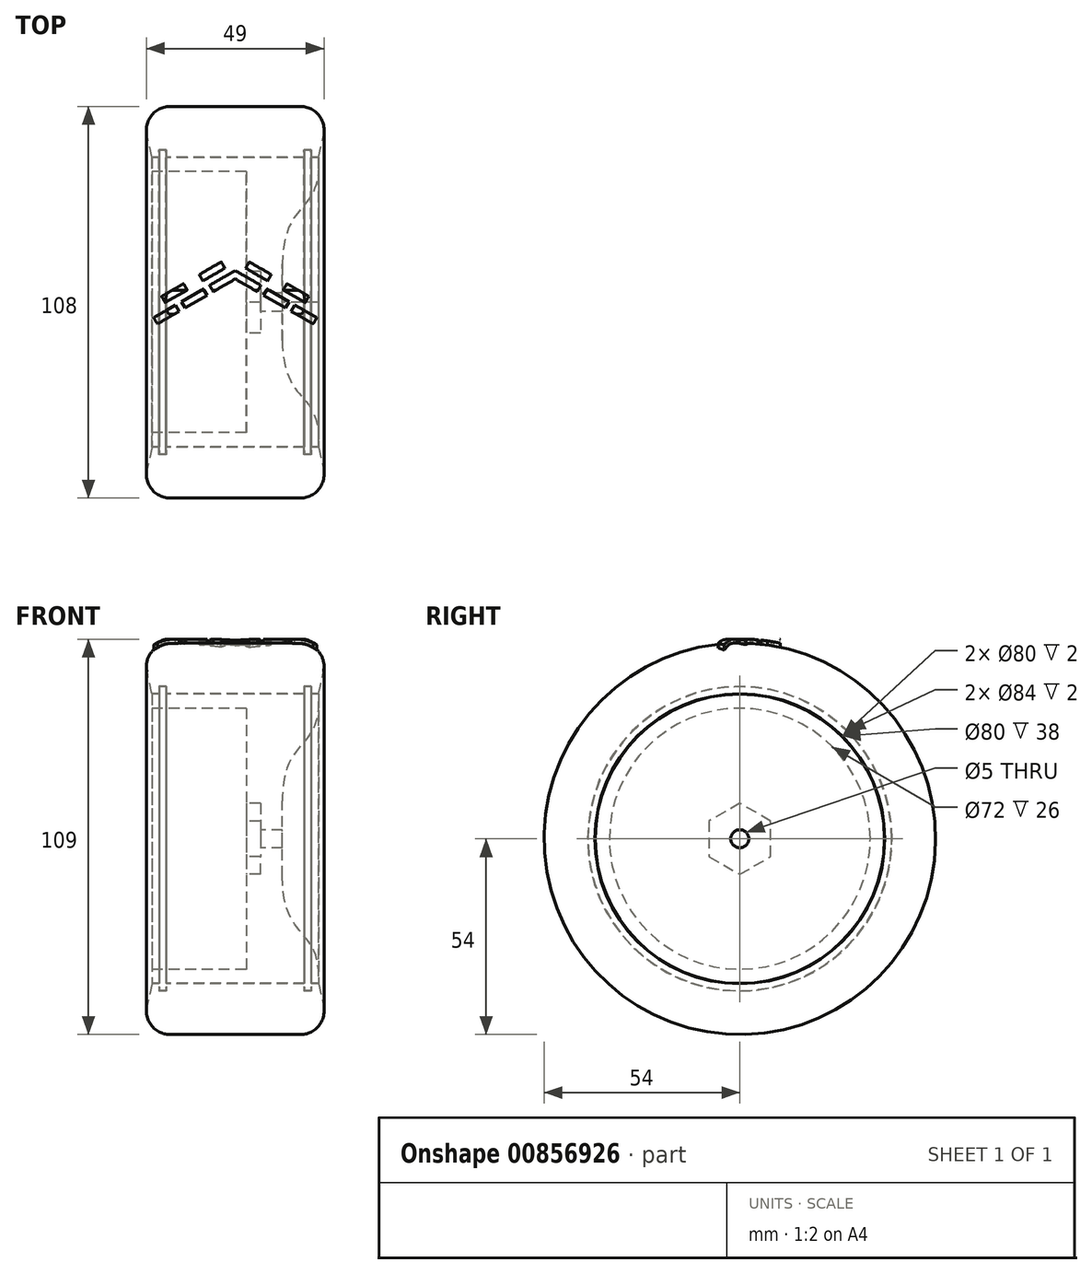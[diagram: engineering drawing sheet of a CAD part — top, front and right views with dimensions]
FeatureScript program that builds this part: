
annotation { "Feature Type Name" : "Feature", "Feature Type Description" : "" }
export const myFeature = defineFeature(function(context is Context, id is Id, definition is map)
    precondition{}
    {
        {
            var Q0;
            Q0=qCreatedBy(makeId("Front.planeOp"),FACE);
            var sketch = newSketch(context, id + "F0", { "sketchPlane" : qUnion([Q0])});
            skLineSegment(sketch, "E0", {"start": v(0, 0) * mm, "end": v(28.5, 0) * mm, "construction": true});
            skLineSegment(sketch, "E1", {"start": v(23, 2.5) * mm, "end": v(3, 2.5) * mm});
            skLineSegment(sketch, "E2", {"start": v(3, 2.5) * mm, "end": v(3, 36) * mm});
            skLineSegment(sketch, "E3", {"start": v(3, 36) * mm, "end": v(-23, 36) * mm});
            skLineSegment(sketch, "E4", {"start": v(-23, 36) * mm, "end": v(-23, 39.9) * mm});
            skLineSegment(sketch, "E5", {"start": v(-15, 54) * mm, "end": v(18, 54) * mm, "construction": true});
            skLineSegment(sketch, "E6", {"start": v(23, 46) * mm, "end": v(23, 40) * mm, "construction": true});
            skLineSegment(sketch, "E7", {"start": v(-23, 40) * mm, "end": v(-21, 40) * mm});
            skLineSegment(sketch, "E8", {"start": v(-21, 40) * mm, "end": v(-21, 42) * mm});
            skLineSegment(sketch, "E9", {"start": v(-21, 42) * mm, "end": v(-19, 42) * mm});
            skLineSegment(sketch, "E10", {"start": v(-19, 42) * mm, "end": v(-19, 40) * mm});
            skLineSegment(sketch, "E11", {"start": v(-19, 40) * mm, "end": v(19, 40) * mm});
            skLineSegment(sketch, "E12", {"start": v(19, 40) * mm, "end": v(19, 42) * mm});
            skLineSegment(sketch, "E13", {"start": v(19, 42) * mm, "end": v(21, 42) * mm});
            skLineSegment(sketch, "E14", {"start": v(21, 42) * mm, "end": v(21, 40) * mm});
            skLineSegment(sketch, "E15", {"start": v(21, 40) * mm, "end": v(23, 40) * mm});
            skLineSegment(sketch, "E16.0", {"start": v(20.9, 39.9) * mm, "end": v(23, 39.9) * mm});
            skLineSegment(sketch, "E16.1", {"start": v(20.9, 41.9) * mm, "end": v(20.9, 39.9) * mm});
            skLineSegment(sketch, "E16.2", {"start": v(19.1, 41.9) * mm, "end": v(20.9, 41.9) * mm});
            skLineSegment(sketch, "E16.3", {"start": v(19.1, 39.9) * mm, "end": v(19.1, 41.9) * mm});
            skLineSegment(sketch, "E16.4", {"start": v(-19.1, 39.9) * mm, "end": v(19.1, 39.9) * mm});
            skLineSegment(sketch, "E16.5", {"start": v(-23, 39.9) * mm, "end": v(-20.9, 39.9) * mm});
            skLineSegment(sketch, "E16.6", {"start": v(-20.9, 39.9) * mm, "end": v(-20.9, 41.9) * mm});
            skLineSegment(sketch, "E16.7", {"start": v(-20.9, 41.9) * mm, "end": v(-19.1, 41.9) * mm});
            skLineSegment(sketch, "E16.8", {"start": v(-19.1, 41.9) * mm, "end": v(-19.1, 39.9) * mm});
            skLineSegment(sketch, "E17.trimOffspring", {"start": v(-23, 40) * mm, "end": v(-23, 46) * mm, "construction": true});
            skLineSegment(sketch, "E18.trimOffspring", {"start": v(23, 39.9) * mm, "end": v(23, 2.5) * mm});
            skPoint(sketch, "E19.visualSharp", {"position": v(-23, 54) * mm});
            skArc(sketch, "E19.filletArc", {"start": v(-15, 54) * mm, "mid": v(-20.66, 51.66) * mm, "end": v(-23, 46) * mm, "construction": true});
            skPoint(sketch, "E20.visualSharp", {"position": v(23, 54) * mm});
            skArc(sketch, "E20.filletArc", {"start": v(23, 46) * mm, "mid": v(20.66, 51.66) * mm, "end": v(15, 54) * mm, "construction": true});
            skLineSegment(sketch, "E21", {"start": v(23, 40) * mm, "end": v(24.35, 46.1) * mm});
            skArc(sketch, "E22", {"start": v(24.35, 46.1) * mm, "mid": v(23.07, 51.57) * mm, "end": v(18, 54) * mm});
            skLineSegment(sketch, "E23", {"start": v(0, 40) * mm, "end": v(0, 59.6) * mm, "construction": true});
            skArc(sketch, "E24.MirrorCS", {"start": v(-24.35, 46.1) * mm, "mid": v(-23.07, 51.57) * mm, "end": v(-18, 54) * mm});
            skLineSegment(sketch, "E25.MirrorCS", {"start": v(-23, 40) * mm, "end": v(-24.35, 46.1) * mm});
            skLineSegment(sketch, "E26", {"start": v(-18, 54) * mm, "end": v(18, 54) * mm});
            skSolve(sketch);
        }
        {
            var Q0;
            Q0=qSketchRegion(id+"F0",true);
            var Q1;
            Q1=sQuery(id+"F0.wireOp",EDGE,"E0");
            revolve(context, id + "F1", {"surfaceOperationType" : NewSurfaceOperationType.NEW, "entities" : qUnion([Q0]), "axis" : qUnion([Q1]), "revolveType" : RevolveType.FULL});
        }
        {
            var Q0;
            Q0=makeQuery(id+"F1.opRevolve","SWEPT_FACE",FACE,{"disambiguationData":[OSD([sQuery(id+"F0.wireOp",EDGE,"E2")])]});
            var sketch = newSketch(context, id + "F2", { "sketchPlane" : qUnion([Q0])});
            skCircle(sketch, "E27.cCircle", {"center": v(0, 0) * mm, "radius": 9.81 * mm, "construction": true});
            skLineSegment(sketch, "E27.0", {"start": v(8.5, 4.9) * mm, "end": v(8.5, -4.9) * mm});
            skLineSegment(sketch, "E27.1", {"start": v(8.5, -4.9) * mm, "end": v(0, -9.81) * mm});
            skLineSegment(sketch, "E27.2", {"start": v(0, -9.81) * mm, "end": v(-8.5, -4.9) * mm});
            skLineSegment(sketch, "E27.3", {"start": v(-8.5, -4.9) * mm, "end": v(-8.5, 4.9) * mm});
            skLineSegment(sketch, "E27.4", {"start": v(-8.5, 4.9) * mm, "end": v(0, 9.81) * mm});
            skLineSegment(sketch, "E27.5", {"start": v(0, 9.81) * mm, "end": v(8.5, 4.9) * mm});
            skSolve(sketch);
        }
        {
            var Q0;
            Q0=qSketchRegion(id+"F2",true);
            extrude(context, id + "F3", {"entities" : qUnion([Q0]), "operationType" : NewBodyOperationType.REMOVE, "oppositeDirection" : true, "depth" : 4 * mm, "offsetDistance" : 25 * mm});
        }
        {
            var Q0;
            Q0=qCreatedBy(makeId("Front.planeOp"),FACE);
            var sketch = newSketch(context, id + "F4", { "sketchPlane" : qUnion([Q0])});
            skLineSegment(sketch, "E28", {"start": v(0, 0) * mm, "end": v(45.35, 0) * mm, "construction": true});
            skLineSegment(sketch, "E29", {"start": v(13, 0) * mm, "end": v(13, 10.5) * mm});
            skLineSegment(sketch, "E30", {"start": v(20.9, 39.9) * mm, "end": v(23, 39.9) * mm, "construction": true});
            skLineSegment(sketch, "E31", {"start": v(23, 39.9) * mm, "end": v(23, 37.9) * mm});
            skFitSpline(sketch, "E32", {"points": [v(23, 37.9) * mm, v(13, 10.5) * mm], "startDerivative": vector(0, -41.43) * mm, "endDerivative": vector(0, -52.48) * mm});
            skLineSegment(sketch, "E33", {"start": v(23, 39.9) * mm, "end": v(24, 39.9) * mm});
            skLineSegment(sketch, "E34", {"start": v(24, 39.9) * mm, "end": v(24, 0) * mm});
            skLineSegment(sketch, "E35", {"start": v(24, 0) * mm, "end": v(13, 0) * mm});
            skSolve(sketch);
        }
        {
            var Q0;
            Q0=makeQuery(id+"F4.imprint","IMPRINT",FACE,{"disambiguationData":[TD([[makeQuery(id+"F4.imprint","IMPRINT",EDGE,{"derivedFrom":sQuery(id+"F4.wireOp",EDGE,"E29")}),-1.0]])]});
            var Q1;
            Q1=sQuery(id+"F4.wireOp",EDGE,"E28");
            revolve(context, id + "F5", {"operationType" : NewBodyOperationType.REMOVE, "surfaceOperationType" : NewSurfaceOperationType.NEW, "entities" : qUnion([Q0]), "axis" : qUnion([Q1]), "revolveType" : RevolveType.FULL, "oppositeDirection" : true});
        }
        {
            var Q0;
            Q0=qCreatedBy(makeId("Top.planeOp"),FACE);
            cPlane(context, id + "F6", {"entities" : qUnion([Q0]), "cplaneType" : CPlaneType.OFFSET, "offset" : (110 / 2) * mm, "width" : 150 * mm, "height" : 150 * mm});
        }
        {
            var Q0;
            Q0=qCreatedBy(id+"F6.planeOp",FACE);
            var sketch = newSketch(context, id + "F7", { "sketchPlane" : qUnion([Q0])});
            skLineSegment(sketch, "E36", {"start": v(-24.5, -48.5) * mm, "end": v(-24.5, 48.5) * mm, "construction": true});
            skLineSegment(sketch, "E37", {"start": v(24.5, -48.5) * mm, "end": v(24.5, 48.5) * mm, "construction": true});
            skLineSegment(sketch, "E38", {"start": v(-24.5, 0) * mm, "end": v(24.5, 0) * mm, "construction": true});
            skLineSegment(sketch, "E39", {"start": v(-21.5, -6) * mm, "end": v(0, 6.41) * mm, "construction": true});
            skLineSegment(sketch, "E40", {"start": v(0, 6.41) * mm, "end": v(21.5, -6) * mm, "construction": true});
            skLineSegment(sketch, "E41", {"start": v(21.5, -6) * mm, "end": v(22.5, -4.27) * mm});
            skLineSegment(sketch, "E42", {"start": v(22.5, -4.27) * mm, "end": v(0, 8.72) * mm, "construction": true});
            skLineSegment(sketch, "E43", {"start": v(0, 8.72) * mm, "end": v(-22.5, -4.27) * mm, "construction": true});
            skLineSegment(sketch, "E44", {"start": v(-22.5, -4.27) * mm, "end": v(-21.5, -6) * mm});
            skLineSegment(sketch, "E45", {"start": v(0, 0) * mm, "end": v(0, 13.9) * mm, "construction": true});
            skLineSegment(sketch, "E46", {"start": v(-21.5, -6) * mm, "end": v(21.5, -6) * mm, "construction": true});
            skLineSegment(sketch, "E47", {"start": v(0, 0) * mm, "end": v(0, -10.86) * mm, "construction": true});
            skLineSegment(sketch, "E48", {"start": v(21.5, -6) * mm, "end": v(15.44, -2.5) * mm});
            skLineSegment(sketch, "E49", {"start": v(15.44, -2.5) * mm, "end": v(16.44, -0.77) * mm});
            skLineSegment(sketch, "E50", {"start": v(16.44, -0.77) * mm, "end": v(22.5, -4.27) * mm});
            skLineSegment(sketch, "E51", {"start": v(-21.5, -6) * mm, "end": v(-15.44, -2.5) * mm});
            skLineSegment(sketch, "E52", {"start": v(-15.44, -2.5) * mm, "end": v(-16.44, -0.77) * mm});
            skLineSegment(sketch, "E53", {"start": v(-16.44, -0.77) * mm, "end": v(-22.5, -4.27) * mm});
            skLineSegment(sketch, "E54", {"start": v(-14.86, 0.15) * mm, "end": v(-13.86, -1.59) * mm});
            skLineSegment(sketch, "E55", {"start": v(-13.86, -1.59) * mm, "end": v(-7.8, 1.91) * mm});
            skLineSegment(sketch, "E56", {"start": v(-7.8, 1.91) * mm, "end": v(-8.8, 3.65) * mm});
            skLineSegment(sketch, "E57", {"start": v(-8.8, 3.65) * mm, "end": v(-14.86, 0.15) * mm});
            skLineSegment(sketch, "E58", {"start": v(8.8, 3.65) * mm, "end": v(7.8, 1.91) * mm});
            skLineSegment(sketch, "E59", {"start": v(7.8, 1.91) * mm, "end": v(13.86, -1.59) * mm});
            skLineSegment(sketch, "E60", {"start": v(13.86, -1.59) * mm, "end": v(14.86, 0.15) * mm});
            skLineSegment(sketch, "E61", {"start": v(14.86, 0.15) * mm, "end": v(8.8, 3.65) * mm});
            skLineSegment(sketch, "E62", {"start": v(7.06, 4.65) * mm, "end": v(6.06, 2.91) * mm});
            skLineSegment(sketch, "E63", {"start": v(6.06, 2.91) * mm, "end": v(0, 6.41) * mm});
            skLineSegment(sketch, "E64", {"start": v(-6.06, 2.91) * mm, "end": v(-7.06, 4.65) * mm});
            skLineSegment(sketch, "E65", {"start": v(-7.06, 4.65) * mm, "end": v(0, 8.72) * mm});
            skLineSegment(sketch, "E66", {"start": v(7.06, 4.65) * mm, "end": v(0, 8.72) * mm});
            skLineSegment(sketch, "E67", {"start": v(-6.06, 2.91) * mm, "end": v(0, 6.41) * mm});
            skLineSegment(sketch, "E68.0", {"start": v(0, 11.03) * mm, "end": v(-23.5, -2.54) * mm, "construction": true});
            skLineSegment(sketch, "E68.1", {"start": v(23.5, -2.54) * mm, "end": v(0, 11.03) * mm, "construction": true});
            skLineSegment(sketch, "E69.0", {"start": v(-1, 12.76) * mm, "end": v(-24.5, -0.8) * mm, "construction": true});
            skLineSegment(sketch, "E70", {"start": v(-20.32, 1.6) * mm, "end": v(-19.32, -0.12) * mm});
            skLineSegment(sketch, "E71", {"start": v(-19.32, -0.12) * mm, "end": v(-13.26, 3.38) * mm});
            skLineSegment(sketch, "E72", {"start": v(-13.26, 3.38) * mm, "end": v(-14.26, 5.1) * mm});
            skLineSegment(sketch, "E73", {"start": v(-14.26, 5.1) * mm, "end": v(-20.32, 1.6) * mm});
            skLineSegment(sketch, "E74", {"start": v(-8.93, 5.88) * mm, "end": v(-9.93, 7.6) * mm});
            skLineSegment(sketch, "E75", {"start": v(-9.93, 7.6) * mm, "end": v(-3.87, 11.1) * mm});
            skLineSegment(sketch, "E76", {"start": v(-3.87, 11.1) * mm, "end": v(-2.87, 9.38) * mm});
            skLineSegment(sketch, "E77", {"start": v(-2.87, 9.38) * mm, "end": v(-8.93, 5.88) * mm});
            skLineSegment(sketch, "E78.MirrorCS", {"start": v(3.87, 11.1) * mm, "end": v(2.87, 9.38) * mm});
            skLineSegment(sketch, "E79.MirrorCS", {"start": v(8.93, 5.88) * mm, "end": v(9.93, 7.6) * mm});
            skLineSegment(sketch, "E80.MirrorCS", {"start": v(13.26, 3.38) * mm, "end": v(14.26, 5.1) * mm});
            skLineSegment(sketch, "E81.MirrorCS", {"start": v(20.32, 1.6) * mm, "end": v(19.32, -0.12) * mm});
            skLineSegment(sketch, "E82", {"start": v(2.87, 9.38) * mm, "end": v(8.93, 5.88) * mm});
            skLineSegment(sketch, "E83", {"start": v(9.93, 7.6) * mm, "end": v(3.87, 11.1) * mm});
            skLineSegment(sketch, "E84", {"start": v(14.26, 5.1) * mm, "end": v(20.32, 1.6) * mm});
            skLineSegment(sketch, "E85", {"start": v(19.32, -0.12) * mm, "end": v(13.26, 3.38) * mm});
            skSolve(sketch);
        }
        {
            var Q0;
            Q0 = qSketchRegion(id + "F7", true);
            extrude(context, id + "F8", {"entities" : qUnion([Q0]), "operationType" : NewBodyOperationType.ADD, "oppositeDirection" : true, "depth" : 5 * mm, "offsetDistance" : 25 * mm});
        }
        {
            var Q0;
            Q0=qCreatedBy(makeId("Front.planeOp"),FACE);
            var sketch = newSketch(context, id + "F9", { "sketchPlane" : qUnion([Q0])});
            skArc(sketch, "E86", {"start": v(-24.35, -46.1) * mm, "mid": v(-24.46, -46.8) * mm, "end": v(-24.5, -47.5) * mm, "construction": true});
            skArc(sketch, "E87", {"start": v(-24.5, 47.5) * mm, "mid": v(-24.46, 46.8) * mm, "end": v(-24.35, 46.1) * mm, "construction": true});
            skArc(sketch, "E88", {"start": v(-24.35, -46.1) * mm, "mid": v(-24.46, -46.8) * mm, "end": v(-24.5, -47.5) * mm});
            skArc(sketch, "E89", {"start": v(-24.5, 47.5) * mm, "mid": v(-24.46, 46.8) * mm, "end": v(-24.35, 46.1) * mm});
            skLineSegment(sketch, "E90", {"start": v(-45.98, 54) * mm, "end": v(37.08, 54) * mm, "construction": true});
            skCircle(sketch, "E91", {"center": v(-18, 47.5) * mm, "radius": 6.5 * mm, "construction": true});
            skArc(sketch, "E92", {"start": v(-18, 55.1) * mm, "mid": v(-23.37, 52.87) * mm, "end": v(-25.6, 47.5) * mm});
            skLineSegment(sketch, "E93", {"start": v(-25.6, 47.5) * mm, "end": v(-29, 47.5) * mm});
            skLineSegment(sketch, "E94", {"start": v(-29, 47.5) * mm, "end": v(-29, 56.1) * mm});
            skArc(sketch, "E95", {"start": v(24.35, 46.1) * mm, "mid": v(24.46, 46.8) * mm, "end": v(24.5, 47.5) * mm, "construction": true});
            skArc(sketch, "E96", {"start": v(25.6, 47.5) * mm, "mid": v(23.37, 52.87) * mm, "end": v(18, 55.1) * mm});
            skLineSegment(sketch, "E97.trimOffspring", {"start": v(-18, 55.1) * mm, "end": v(18, 55.1) * mm});
            skLineSegment(sketch, "E98", {"start": v(25.6, 47.5) * mm, "end": v(29, 47.5) * mm});
            skLineSegment(sketch, "E99", {"start": v(29, 47.5) * mm, "end": v(29, 56.1) * mm});
            skLineSegment(sketch, "E100", {"start": v(29, 56.1) * mm, "end": v(-29, 56.1) * mm});
            skLineSegment(sketch, "E101", {"start": v(0, 0) * mm, "end": v(60.16, 0) * mm, "construction": true});
            skSolve(sketch);
        }
        {
            var Q0;
            Q0=makeQuery(id+"F9.imprint","IMPRINT",FACE,{"disambiguationData":[TD([[makeQuery(id+"F9.imprint","IMPRINT",EDGE,{"derivedFrom":sQuery(id+"F9.wireOp",EDGE,"E92")}),-1.0]])]});
            var Q1;
            Q1 = qConstructionFilter(qBodyType(qCreatedBy(id + "F9" ,EDGE), BodyType.WIRE), ConstructionObject.NO);
            var Q2;
            Q2=sQuery(id+"F9.wireOp",EDGE,"E101");
            revolve(context, id + "F10", {"operationType" : NewBodyOperationType.REMOVE, "surfaceOperationType" : NewSurfaceOperationType.NEW, "entities" : qUnion([Q0]), "surfaceEntities" : qUnion([Q1]), "axis" : qUnion([Q2]), "revolveType" : RevolveType.FULL, "oppositeDirection" : true});
        }
    });
